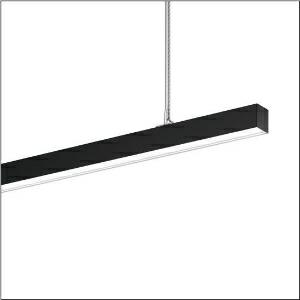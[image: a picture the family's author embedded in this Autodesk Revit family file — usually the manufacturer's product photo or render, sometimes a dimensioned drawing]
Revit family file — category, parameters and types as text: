
# Revit family: silica_21_51mx30tct9b
name_source: partatom
category: Lighting Fixtures
units: mm (PartAtom-declared; Revit-internal decimal feet)

## family parameters
Cut with Voids When Loaded = No
Host = Face
Light Source = No
Part Type = Normal
Room Calculation Point = No
Round Connector Dimension = Use Diameter
Shared = No

## types (1)
- --- (1 x LED, 10300 lm, 84.4 W, 6500K)
    Apparent Load = 84 VA
    CIE Flux Codes = 47 79 96 58 100
    Color Rendering = 80
    Color Temperature = 6500K
    Default Elevation = 1800 mm
    Description = Silica 21, office luminaire, primary optical cover: cover, of PMMA, opal, light emission: direct/indirect distribution, primary light characteristic: symmetric, installation type: suspended mounting, LED, rated luminous flux: 10.300lm, luminous efficacy: 116lm/W, light colour: 8tw, colour temperature: 2700..6500K, control gear: DALI DT8, with terminal, 3+2-pole, max. 2.5mm², mains connection: 220..240V, AC, 50/60Hz, rated input power: 88.7W, luminaire housing, of aluminium, matt jet black (RAL 9005), length: 3.004mm, width: 53mm, height: 53mm, protection rating (complete): IP20, insulation class (complete): insulation class I (protective earthing), certification: CE, permissible operating ambient temperature: 0..+35°C, standard: EN 50419, packaging unit: 1 piece
    Height = 53 mm
    Lamp = 1 x LED
    Lamp Light Flux = 10300 lm
    Lamp Power = 84.4 W
    Lamp count = 1
    Length = 3004 mm
    Luminous efficacy = 122 lm/W
    Manufacturer = Siteco
    ModVariant = No
    Model = 51MX30TCT9B
    Mounting Place = Ceiling
    Mounting Type = Pendant
    Number of Poles = 1
    OnlyDefault = Yes
    Power Factor = 1
    Product Name = Silica 21
    Product group = office luminaire | ceiling pendant
    ProductGroupID = 903
    Protection Class = Protection class I
    Protection Degree = IP 20
    RLX_Detail_Level = 1
    RLX_Emergency_Light_Flux = 0 lm
    RLX_Emergency_Type = 0
    RLX_Emergency_Type_DB = No
    RlxData = <blob elided: 22737 chars, md5=62e7c297>
    Socket = socket
    Standby Power = 0 W
    System Light Flux = 10300 lm
    System Power = 84 W
    Type Comments = individual setting
    Type Image = l_1335856.jpg
    URL = http://relux.com
    VarID = @adj_139121
    Voltage = 0 V
    Weight = 0.00 kg
    Width = 53 mm

## geometry (parser evidence)
native form markers: Blend x4, Sweep x14
no freeform markers — native parametric forms only
